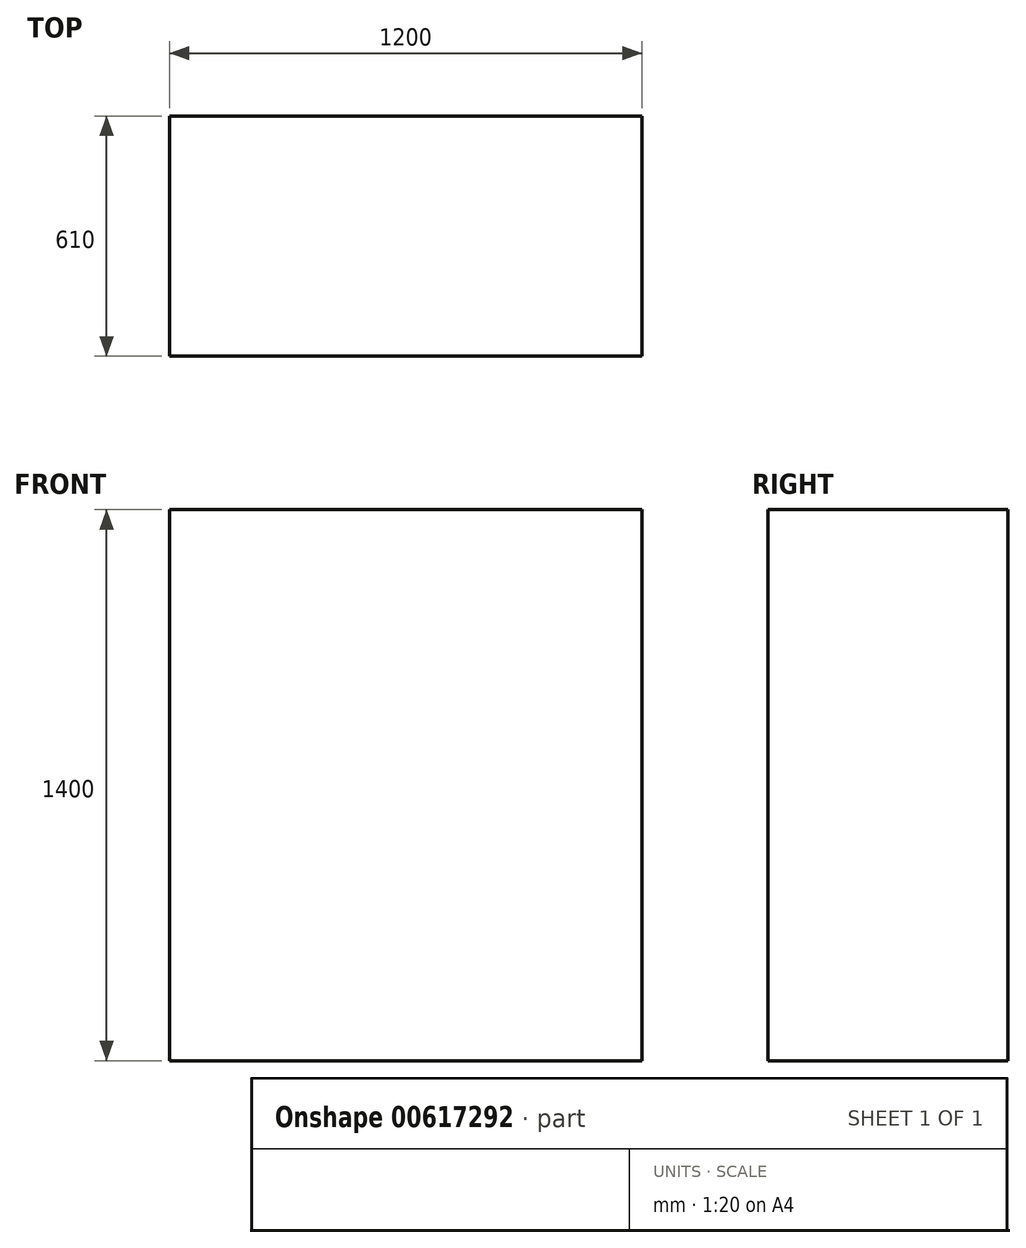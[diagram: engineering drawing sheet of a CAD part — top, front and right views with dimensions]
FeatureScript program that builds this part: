
annotation { "Feature Type Name" : "Feature", "Feature Type Description" : "" }
export const myFeature = defineFeature(function(context is Context, id is Id, definition is map)
    precondition{}
    {
        {
            var Q0;
            Q0=qCreatedBy(makeId("Top.planeOp"),FACE);
            var sketch = newSketch(context, id + "F0", { "sketchPlane" : qUnion([Q0])});
            skLineSegment(sketch, "E0.bottom", {"start": v(-497.78, 309.61) * mm, "end": v(702.22, 309.61) * mm});
            skLineSegment(sketch, "E0.top", {"start": v(-497.78, -300.39) * mm, "end": v(702.22, -300.39) * mm});
            skLineSegment(sketch, "E0.left", {"start": v(-497.78, 309.61) * mm, "end": v(-497.78, -300.39) * mm});
            skLineSegment(sketch, "E0.right", {"start": v(702.22, 309.61) * mm, "end": v(702.22, -300.39) * mm});
            skSolve(sketch);
        }
        {
            var Q0;
            Q0=qSketchRegion(id+"F0",true);
            extrude(context, id + "F1", {"entities" : qUnion([Q0]), "depth" : 1400 * mm, "offsetDistance" : 25 * mm});
        }
    });
